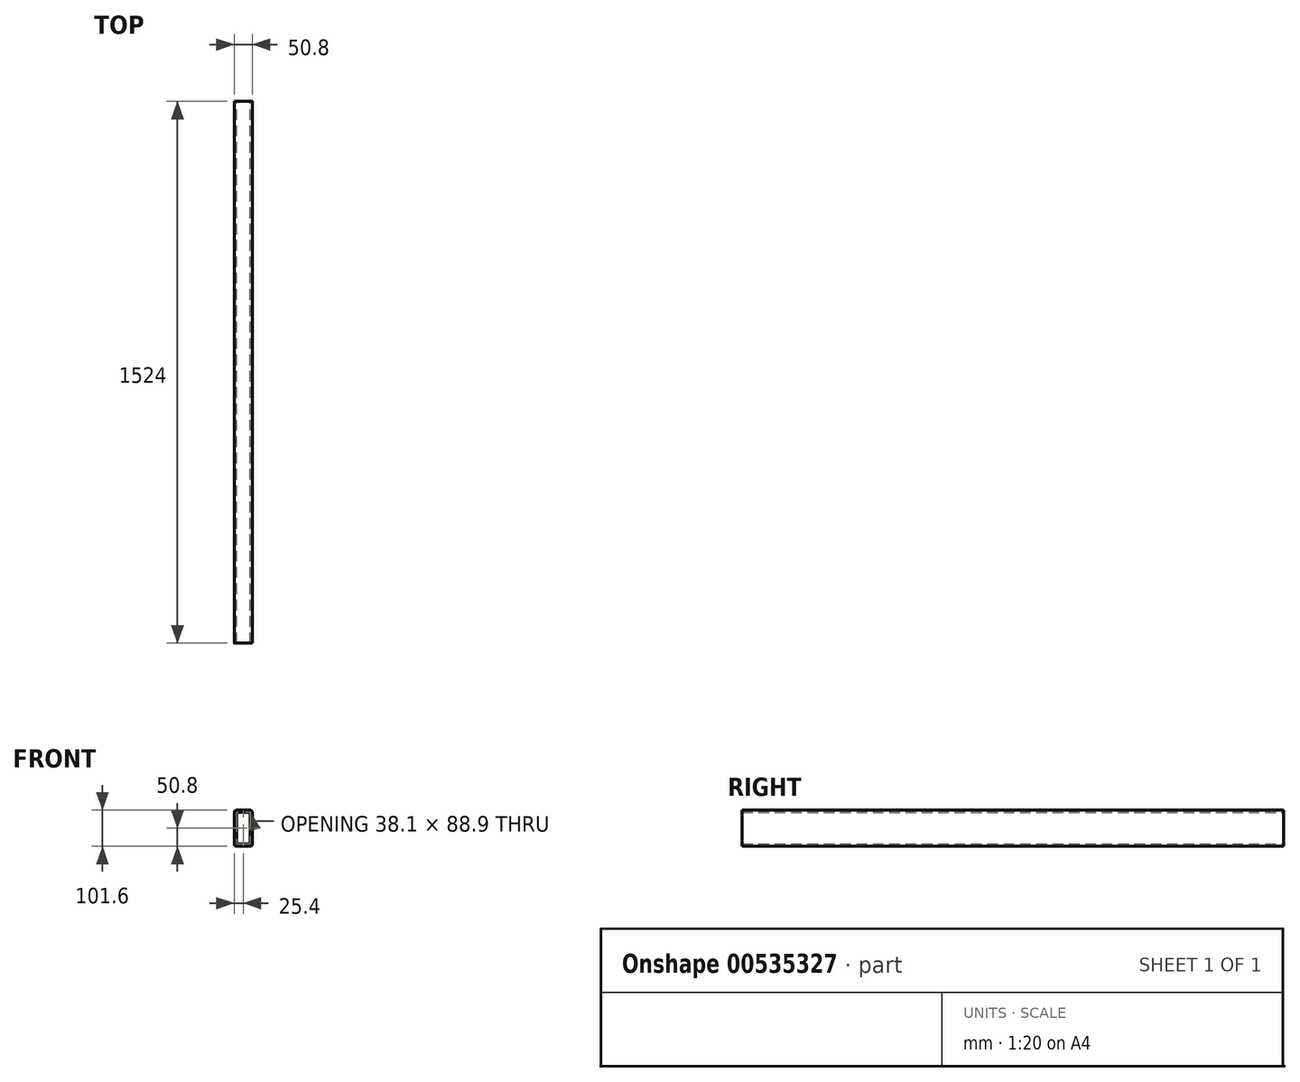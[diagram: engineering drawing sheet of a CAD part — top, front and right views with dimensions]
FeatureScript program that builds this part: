
annotation { "Feature Type Name" : "Feature", "Feature Type Description" : "" }
export const myFeature = defineFeature(function(context is Context, id is Id, definition is map)
    precondition{}
    {
        {
            var Q0;
            Q0=qCreatedBy(makeId("Front.planeOp"),FACE);
            var sketch = newSketch(context, id + "F0", { "sketchPlane" : qUnion([Q0])});
            skLineSegment(sketch, "E0.bottom", {"start": v(19.05, 50.8) * mm, "end": v(-19.05, 50.8) * mm});
            skLineSegment(sketch, "E0.top", {"start": v(19.05, -50.8) * mm, "end": v(-19.05, -50.8) * mm});
            skLineSegment(sketch, "E0.left", {"start": v(25.4, 44.45) * mm, "end": v(25.4, -44.45) * mm});
            skLineSegment(sketch, "E0.right", {"start": v(-25.4, 44.45) * mm, "end": v(-25.4, -44.45) * mm});
            skPoint(sketch, "E1.visualSharp", {"position": v(-25.4, 50.8) * mm});
            skArc(sketch, "E1.filletArc", {"start": v(-19.05, 50.8) * mm, "mid": v(-23.54, 48.94) * mm, "end": v(-25.4, 44.45) * mm});
            skPoint(sketch, "E2.visualSharp", {"position": v(-25.4, -50.8) * mm});
            skArc(sketch, "E2.filletArc", {"start": v(-25.4, -44.45) * mm, "mid": v(-23.54, -48.94) * mm, "end": v(-19.05, -50.8) * mm});
            skPoint(sketch, "E3.visualSharp", {"position": v(25.4, -50.8) * mm});
            skArc(sketch, "E3.filletArc", {"start": v(19.05, -50.8) * mm, "mid": v(23.54, -48.94) * mm, "end": v(25.4, -44.45) * mm});
            skPoint(sketch, "E4.visualSharp", {"position": v(25.4, 50.8) * mm});
            skArc(sketch, "E4.filletArc", {"start": v(25.4, 44.45) * mm, "mid": v(23.54, 48.94) * mm, "end": v(19.05, 50.8) * mm});
            skLineSegment(sketch, "E5.bottom", {"start": v(15.88, 44.45) * mm, "end": v(-15.88, 44.45) * mm});
            skLineSegment(sketch, "E5.top", {"start": v(15.88, -44.45) * mm, "end": v(-15.88, -44.45) * mm});
            skLineSegment(sketch, "E5.left", {"start": v(19.05, 41.28) * mm, "end": v(19.05, -41.28) * mm});
            skLineSegment(sketch, "E5.right", {"start": v(-19.05, 41.28) * mm, "end": v(-19.05, -41.28) * mm});
            skPoint(sketch, "E5.middle", {"position": v(0, 0) * mm});
            skArc(sketch, "E6.filletArc", {"start": v(-15.88, 44.45) * mm, "mid": v(-18.12, 43.52) * mm, "end": v(-19.05, 41.28) * mm});
            skArc(sketch, "E7.filletArc", {"start": v(19.05, 41.28) * mm, "mid": v(18.12, 43.52) * mm, "end": v(15.88, 44.45) * mm});
            skArc(sketch, "E8.filletArc", {"start": v(-19.05, -41.28) * mm, "mid": v(-18.12, -43.52) * mm, "end": v(-15.88, -44.45) * mm});
            skArc(sketch, "E9.filletArc", {"start": v(15.88, -44.45) * mm, "mid": v(18.12, -43.52) * mm, "end": v(19.05, -41.28) * mm});
            skLineSegment(sketch, "E10", {"start": v(-19.05, 44.45) * mm, "end": v(19.05, -44.45) * mm, "construction": true});
            skLineSegment(sketch, "E11", {"start": v(19.05, 44.45) * mm, "end": v(-19.05, -44.45) * mm, "construction": true});
            skSolve(sketch);
        }
        {
            var Q0;
            Q0 = qSketchRegion(id + "F0", true);
            extrude(context, id + "F1", {"entities" : qUnion([Q0]), "endBound" : BoundingType.SYMMETRIC, "depth" : 1524 * mm, "offsetDistance" : 25.4 * mm});
        }
    });
